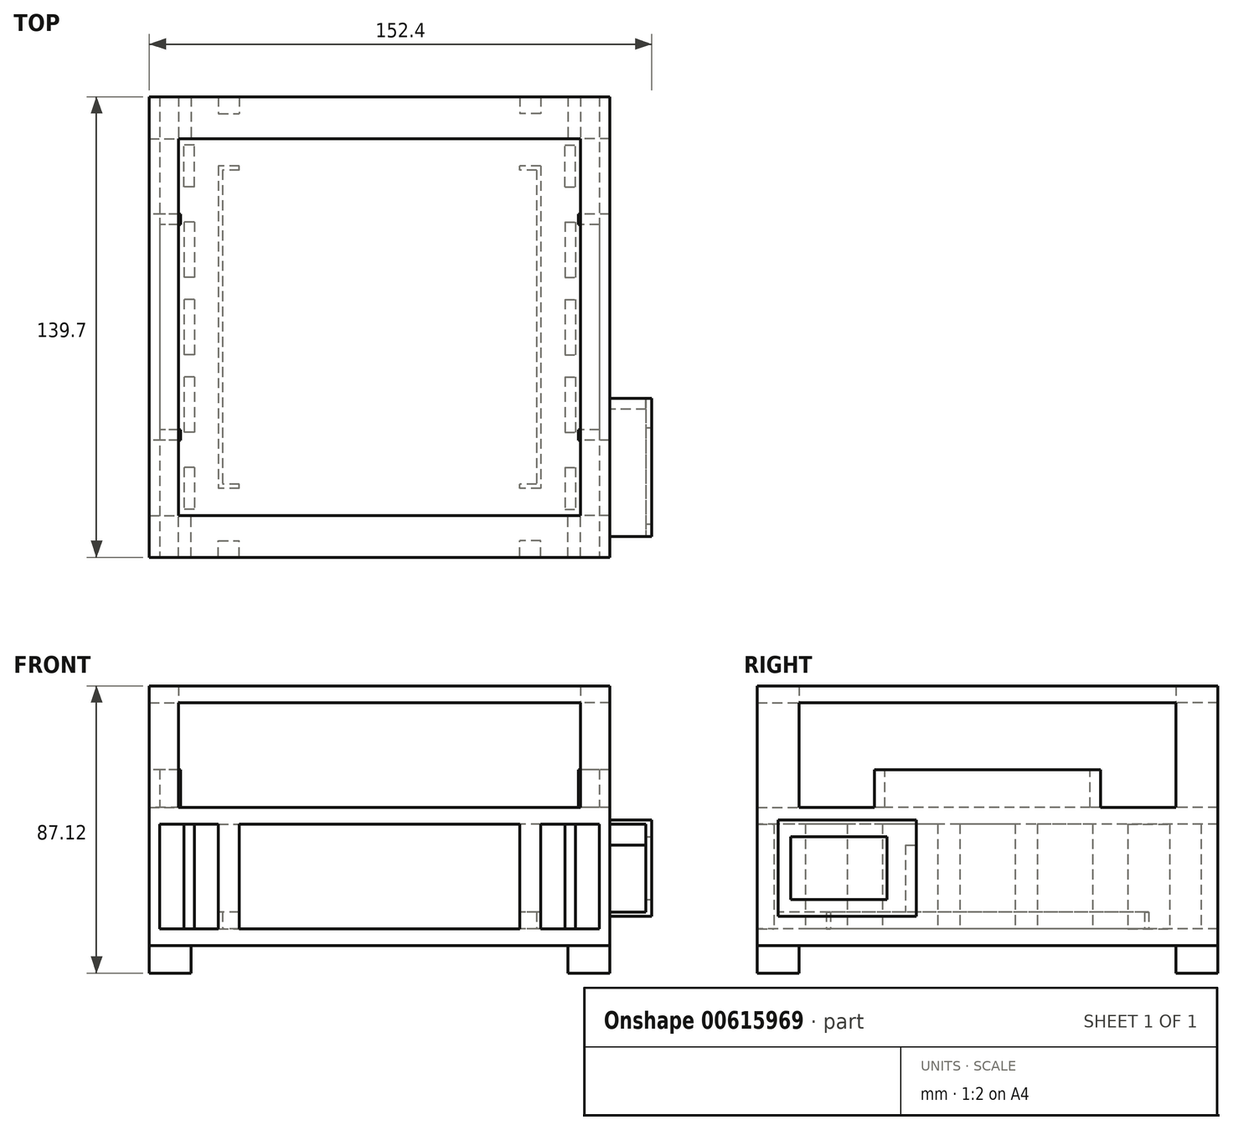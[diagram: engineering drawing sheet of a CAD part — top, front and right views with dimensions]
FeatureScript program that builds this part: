
annotation { "Feature Type Name" : "Feature", "Feature Type Description" : "" }
export const myFeature = defineFeature(function(context is Context, id is Id, definition is map)
    precondition{}
    {
        {
            var Q0;
            Q0=qCreatedBy(makeId("Top.planeOp"),FACE);
            var sketch = newSketch(context, id + "F0", { "sketchPlane" : qUnion([Q0])});
            skLineSegment(sketch, "E0.bottom", {"start": v(69.85, 69.85) * mm, "end": v(-69.85, 69.85) * mm, "construction": true});
            skLineSegment(sketch, "E0.top", {"start": v(69.85, -69.85) * mm, "end": v(-69.85, -69.85) * mm, "construction": true});
            skLineSegment(sketch, "E0.left", {"start": v(69.85, 69.85) * mm, "end": v(69.85, -69.85) * mm, "construction": true});
            skLineSegment(sketch, "E0.right", {"start": v(-69.85, 69.85) * mm, "end": v(-69.85, -69.85) * mm, "construction": true});
            skPoint(sketch, "E0.middle", {"position": v(0, 0) * mm});
            skLineSegment(sketch, "E1.bottom", {"start": v(-69.85, -69.85) * mm, "end": v(-57.15, -69.85) * mm});
            skLineSegment(sketch, "E1.top", {"start": v(-69.85, -57.15) * mm, "end": v(-57.15, -57.15) * mm});
            skLineSegment(sketch, "E1.left", {"start": v(-69.85, -69.85) * mm, "end": v(-69.85, -57.15) * mm});
            skLineSegment(sketch, "E1.right", {"start": v(-57.15, -69.85) * mm, "end": v(-57.15, -57.15) * mm});
            skLineSegment(sketch, "E2.bottom", {"start": v(69.85, -69.85) * mm, "end": v(57.15, -69.85) * mm});
            skLineSegment(sketch, "E2.top", {"start": v(69.85, -57.15) * mm, "end": v(57.15, -57.15) * mm});
            skLineSegment(sketch, "E2.left", {"start": v(69.85, -69.85) * mm, "end": v(69.85, -57.15) * mm});
            skLineSegment(sketch, "E2.right", {"start": v(57.15, -69.85) * mm, "end": v(57.15, -57.15) * mm});
            skLineSegment(sketch, "E3.bottom", {"start": v(69.85, 69.85) * mm, "end": v(57.15, 69.85) * mm});
            skLineSegment(sketch, "E3.top", {"start": v(69.85, 57.15) * mm, "end": v(57.15, 57.15) * mm});
            skLineSegment(sketch, "E3.left", {"start": v(69.85, 69.85) * mm, "end": v(69.85, 57.15) * mm});
            skLineSegment(sketch, "E3.right", {"start": v(57.15, 69.85) * mm, "end": v(57.15, 57.15) * mm});
            skLineSegment(sketch, "E4.bottom", {"start": v(-69.85, 69.85) * mm, "end": v(-57.15, 69.85) * mm});
            skLineSegment(sketch, "E4.top", {"start": v(-69.85, 57.15) * mm, "end": v(-57.15, 57.15) * mm});
            skLineSegment(sketch, "E4.left", {"start": v(-69.85, 69.85) * mm, "end": v(-69.85, 57.15) * mm});
            skLineSegment(sketch, "E4.right", {"start": v(-57.15, 69.85) * mm, "end": v(-57.15, 57.15) * mm});
            skSolve(sketch);
        }
        {
            var Q0;
            Q0=qSketchRegion(id+"F0",true);
            extrude(context, id + "F1", {"entities" : qUnion([Q0]), "depth" : 8.38 * mm});
        }
        {
            var Q0;
            Q0=makeQuery(id+"F1.opExtrude","CAP_FACE",FACE,{"disambiguationData":[OSD([sQuery(id+"F0.wireOp",EDGE,"E1.bottom"),sQuery(id+"F0.wireOp",EDGE,"E1.top"),sQuery(id+"F0.wireOp",EDGE,"E1.left"),sQuery(id+"F0.wireOp",EDGE,"E1.right")])],"isStart":false});
            var sketch = newSketch(context, id + "F2", { "sketchPlane" : qUnion([Q0])});
            skLineSegment(sketch, "E5.bottom", {"start": v(-69.85, -69.85) * mm, "end": v(69.85, -69.85) * mm});
            skLineSegment(sketch, "E5.top", {"start": v(-69.85, 69.85) * mm, "end": v(69.85, 69.85) * mm});
            skLineSegment(sketch, "E5.left", {"start": v(-69.85, -69.85) * mm, "end": v(-69.85, 69.85) * mm});
            skLineSegment(sketch, "E5.right", {"start": v(69.85, -69.85) * mm, "end": v(69.85, 69.85) * mm});
            skSolve(sketch);
        }
        {
            var Q0;
            Q0=qSketchRegion(id+"F2",true);
            extrude(context, id + "F3", {"entities" : qUnion([Q0]), "depth" : 5.08 * mm});
        }
        {
            var Q0;
            Q0=makeQuery(id+"F3.opExtrude","CAP_FACE",FACE,{"disambiguationData":[OSD([sQuery(id+"F2.wireOp",EDGE,"E5.bottom"),sQuery(id+"F2.wireOp",EDGE,"E5.top"),sQuery(id+"F2.wireOp",EDGE,"E5.left"),sQuery(id+"F2.wireOp",EDGE,"E5.right")])],"isStart":false});
            var sketch = newSketch(context, id + "F4", { "sketchPlane" : qUnion([Q0])});
            skSolve(sketch);
        }
        {
            var Q0;
            Q0=makeQuery(id+"F4.imprint","IMPRINT",FACE,{"disambiguationData":[TD([[makeQuery(id+"F4.imprint","IMPRINT",EDGE,{"derivedFrom":makeQuery(id+"F3.opExtrude","CAP_EDGE",EDGE,{"disambiguationData":[OSD([sQuery(id+"F2.wireOp",EDGE,"E5.bottom")])],"isStart":false})}),1.0]])]});
            var sketch = newSketch(context, id + "F5", { "sketchPlane" : qUnion([Q0])});
            skLineSegment(sketch, "E6.bottom", {"start": v(47.62, 47.63) * mm, "end": v(-47.63, 47.63) * mm});
            skLineSegment(sketch, "E6.top", {"start": v(47.63, -47.63) * mm, "end": v(-47.62, -47.63) * mm});
            skLineSegment(sketch, "E6.left", {"start": v(47.62, 47.63) * mm, "end": v(47.63, -47.63) * mm});
            skLineSegment(sketch, "E6.right", {"start": v(-47.63, 47.63) * mm, "end": v(-47.62, -47.63) * mm});
            skPoint(sketch, "E6.middle", {"position": v(0, 0) * mm});
            skLineSegment(sketch, "E7.bottom", {"start": v(48.9, 48.9) * mm, "end": v(-48.9, 48.9) * mm});
            skLineSegment(sketch, "E7.top", {"start": v(48.9, -48.9) * mm, "end": v(-48.9, -48.9) * mm});
            skLineSegment(sketch, "E7.left", {"start": v(48.9, 48.9) * mm, "end": v(48.9, -48.9) * mm});
            skLineSegment(sketch, "E7.right", {"start": v(-48.9, 48.9) * mm, "end": v(-48.9, -48.9) * mm});
            skSolve(sketch);
        }
        {
            var Q0;
            Q0=qSketchRegion(id+"F5",true);
            extrude(context, id + "F6", {"entities" : qUnion([Q0]), "operationType" : NewBodyOperationType.ADD, "depth" : 5.08 * mm});
        }
        {
            var Q0;
            Q0=makeQuery(id+"F4.imprint","IMPRINT",FACE,{"disambiguationData":[TD([[makeQuery(id+"F4.imprint","IMPRINT",EDGE,{"derivedFrom":makeQuery(id+"F3.opExtrude","CAP_EDGE",EDGE,{"disambiguationData":[OSD([sQuery(id+"F2.wireOp",EDGE,"E5.bottom")])],"isStart":false})}),1.0]])]});
            var sketch = newSketch(context, id + "F7", { "sketchPlane" : qUnion([Q0])});
            skLineSegment(sketch, "E8.bottom", {"start": v(42.55, -69.85) * mm, "end": v(-42.54, -69.85) * mm});
            skLineSegment(sketch, "E8.top", {"start": v(42.54, 69.85) * mm, "end": v(-42.55, 69.85) * mm});
            skLineSegment(sketch, "E8.left", {"start": v(42.55, -69.85) * mm, "end": v(42.54, 69.85) * mm});
            skLineSegment(sketch, "E8.right", {"start": v(-42.54, -69.85) * mm, "end": v(-42.55, 69.85) * mm});
            skPoint(sketch, "E8.middle", {"position": v(0, 0) * mm});
            skSolve(sketch);
        }
        {
            var Q0;
            Q0=qSketchRegion(id+"F7",true);
            extrude(context, id + "F8", {"entities" : qUnion([Q0]), "operationType" : NewBodyOperationType.REMOVE, "depth" : 5.08 * mm});
        }
        {
            var Q0;
            Q0=makeQuery(id+"F4.imprint","IMPRINT",FACE,{"disambiguationData":[TD([[makeQuery(id+"F4.imprint","IMPRINT",EDGE,{"derivedFrom":makeQuery(id+"F3.opExtrude","CAP_EDGE",EDGE,{"disambiguationData":[OSD([sQuery(id+"F2.wireOp",EDGE,"E5.bottom")])],"isStart":false})}),1.0]])]});
            var sketch = newSketch(context, id + "F9", { "sketchPlane" : qUnion([Q0])});
            skLineSegment(sketch, "E9.bottom", {"start": v(69.85, 69.85) * mm, "end": v(-69.85, 69.85) * mm, "construction": true});
            skLineSegment(sketch, "E9.top", {"start": v(69.85, -69.85) * mm, "end": v(-69.85, -69.85) * mm, "construction": true});
            skLineSegment(sketch, "E9.left", {"start": v(69.85, 69.85) * mm, "end": v(69.85, -69.85) * mm, "construction": true});
            skLineSegment(sketch, "E9.right", {"start": v(-69.85, 69.85) * mm, "end": v(-69.85, -69.85) * mm, "construction": true});
            skPoint(sketch, "E9.middle", {"position": v(0, 0) * mm});
            skLineSegment(sketch, "E10.bottom", {"start": v(-69.85, 69.85) * mm, "end": v(-66.68, 69.85) * mm});
            skLineSegment(sketch, "E10.top", {"start": v(-69.85, -69.85) * mm, "end": v(-66.67, -69.85) * mm});
            skLineSegment(sketch, "E10.left", {"start": v(-69.85, 69.85) * mm, "end": v(-69.85, -69.85) * mm});
            skLineSegment(sketch, "E10.right", {"start": v(-66.68, 69.85) * mm, "end": v(-66.67, -69.85) * mm});
            skLineSegment(sketch, "E11.bottom", {"start": v(-48.9, -48.9) * mm, "end": v(-66.67, -48.9) * mm, "construction": true});
            skLineSegment(sketch, "E11.top", {"start": v(-48.9, 48.9) * mm, "end": v(-66.67, 48.9) * mm, "construction": true});
            skLineSegment(sketch, "E11.left", {"start": v(-48.9, -48.9) * mm, "end": v(-48.9, 48.9) * mm, "construction": true});
            skLineSegment(sketch, "E11.right", {"start": v(-66.68, -48.9) * mm, "end": v(-66.68, 48.9) * mm, "construction": true});
            skLineSegment(sketch, "E12.bottom", {"start": v(-66.67, 48.9) * mm, "end": v(-57.78, 48.9) * mm, "construction": true});
            skLineSegment(sketch, "E12.top", {"start": v(-66.67, -48.9) * mm, "end": v(-57.78, -48.9) * mm, "construction": true});
            skLineSegment(sketch, "E12.left", {"start": v(-66.68, 48.9) * mm, "end": v(-66.68, -48.9) * mm, "construction": true});
            skLineSegment(sketch, "E12.right", {"start": v(-57.78, 48.9) * mm, "end": v(-57.78, -48.9) * mm, "construction": true});
            skLineSegment(sketch, "E13.bottom", {"start": v(-66.67, 48.9) * mm, "end": v(-48.9, 48.9) * mm, "construction": true});
            skLineSegment(sketch, "E13.top", {"start": v(-66.67, 23.5) * mm, "end": v(-48.9, 23.5) * mm, "construction": true});
            skLineSegment(sketch, "E13.left", {"start": v(-66.68, 48.9) * mm, "end": v(-66.68, 23.5) * mm, "construction": true});
            skLineSegment(sketch, "E13.right", {"start": v(-48.9, 48.9) * mm, "end": v(-48.9, 23.5) * mm, "construction": true});
            skLineSegment(sketch, "E14.bottom", {"start": v(-66.67, -48.9) * mm, "end": v(-48.9, -48.9) * mm, "construction": true});
            skLineSegment(sketch, "E14.top", {"start": v(-66.67, -23.5) * mm, "end": v(-48.9, -23.5) * mm, "construction": true});
            skLineSegment(sketch, "E14.left", {"start": v(-66.68, -48.9) * mm, "end": v(-66.68, -23.5) * mm, "construction": true});
            skLineSegment(sketch, "E14.right", {"start": v(-48.9, -48.9) * mm, "end": v(-48.9, -23.5) * mm, "construction": true});
            skLineSegment(sketch, "E15.bottom", {"start": v(-56.2, 31.88) * mm, "end": v(-59.37, 31.88) * mm});
            skLineSegment(sketch, "E15.top", {"start": v(-56.2, 15.11) * mm, "end": v(-59.37, 15.11) * mm});
            skLineSegment(sketch, "E15.left", {"start": v(-56.2, 31.88) * mm, "end": v(-56.2, 15.11) * mm});
            skLineSegment(sketch, "E15.right", {"start": v(-59.37, 31.88) * mm, "end": v(-59.37, 15.11) * mm});
            skPoint(sketch, "E15.middle", {"position": v(-57.78, 23.5) * mm});
            skLineSegment(sketch, "E16.bottom", {"start": v(-56.2, 8.38) * mm, "end": v(-59.37, 8.38) * mm});
            skLineSegment(sketch, "E16.top", {"start": v(-56.2, -8.38) * mm, "end": v(-59.37, -8.38) * mm});
            skLineSegment(sketch, "E16.left", {"start": v(-56.2, 8.38) * mm, "end": v(-56.2, -8.38) * mm});
            skLineSegment(sketch, "E16.right", {"start": v(-59.37, 8.38) * mm, "end": v(-59.37, -8.38) * mm});
            skPoint(sketch, "E16.middle", {"position": v(-57.78, 0) * mm});
            skLineSegment(sketch, "E17.bottom", {"start": v(-56.2, -15.11) * mm, "end": v(-59.37, -15.11) * mm});
            skLineSegment(sketch, "E17.top", {"start": v(-56.2, -31.88) * mm, "end": v(-59.37, -31.88) * mm});
            skLineSegment(sketch, "E17.left", {"start": v(-56.2, -15.11) * mm, "end": v(-56.2, -31.88) * mm});
            skLineSegment(sketch, "E17.right", {"start": v(-59.37, -15.11) * mm, "end": v(-59.37, -31.88) * mm});
            skPoint(sketch, "E17.middle", {"position": v(-57.78, -23.5) * mm});
            skLineSegment(sketch, "E18.bottom", {"start": v(-56.2, 42.55) * mm, "end": v(-59.37, 42.55) * mm});
            skLineSegment(sketch, "E18.top", {"start": v(-56.2, 55.25) * mm, "end": v(-59.37, 55.25) * mm});
            skLineSegment(sketch, "E18.left", {"start": v(-56.2, 42.55) * mm, "end": v(-56.2, 55.25) * mm});
            skLineSegment(sketch, "E18.right", {"start": v(-59.37, 42.55) * mm, "end": v(-59.37, 55.25) * mm});
            skPoint(sketch, "E18.middle", {"position": v(-57.78, 48.9) * mm});
            skLineSegment(sketch, "E19.bottom", {"start": v(-56.2, -42.55) * mm, "end": v(-59.37, -42.55) * mm});
            skLineSegment(sketch, "E19.top", {"start": v(-56.2, -55.25) * mm, "end": v(-59.37, -55.25) * mm});
            skLineSegment(sketch, "E19.left", {"start": v(-56.2, -42.55) * mm, "end": v(-56.2, -55.25) * mm});
            skLineSegment(sketch, "E19.right", {"start": v(-59.37, -42.55) * mm, "end": v(-59.37, -55.25) * mm});
            skPoint(sketch, "E19.middle", {"position": v(-57.78, -48.9) * mm});
            skLineSegment(sketch, "E20.bottom", {"start": v(-48.9, 69.85) * mm, "end": v(-42.55, 69.85) * mm});
            skLineSegment(sketch, "E20.top", {"start": v(-48.9, 64.77) * mm, "end": v(-42.55, 64.77) * mm});
            skLineSegment(sketch, "E20.left", {"start": v(-48.9, 69.85) * mm, "end": v(-48.9, 64.77) * mm});
            skLineSegment(sketch, "E20.right", {"start": v(-42.55, 69.85) * mm, "end": v(-42.55, 64.77) * mm});
            skLineSegment(sketch, "E21.bottom", {"start": v(-48.9, -69.85) * mm, "end": v(-42.55, -69.85) * mm});
            skLineSegment(sketch, "E21.top", {"start": v(-48.9, -64.77) * mm, "end": v(-42.55, -64.77) * mm});
            skLineSegment(sketch, "E21.left", {"start": v(-48.9, -69.85) * mm, "end": v(-48.9, -64.77) * mm});
            skLineSegment(sketch, "E21.right", {"start": v(-42.55, -69.85) * mm, "end": v(-42.55, -64.77) * mm});
            skLineSegment(sketch, "E22", {"start": v(0, 69.85) * mm, "end": v(0, -69.85) * mm, "construction": true});
            skLineSegment(sketch, "E23.MirrorCS", {"start": v(56.2, 42.55) * mm, "end": v(56.2, 55.25) * mm});
            skLineSegment(sketch, "E24.MirrorCS", {"start": v(42.55, 69.85) * mm, "end": v(42.55, 64.77) * mm});
            skLineSegment(sketch, "E25.MirrorCS", {"start": v(56.2, -55.25) * mm, "end": v(59.37, -55.25) * mm});
            skLineSegment(sketch, "E26.MirrorCS", {"start": v(56.2, 15.11) * mm, "end": v(59.37, 15.11) * mm});
            skLineSegment(sketch, "E27.MirrorCS", {"start": v(48.9, -69.85) * mm, "end": v(48.9, -64.77) * mm});
            skLineSegment(sketch, "E28.MirrorCS", {"start": v(42.55, -69.85) * mm, "end": v(42.55, -64.77) * mm});
            skLineSegment(sketch, "E29.MirrorCS", {"start": v(66.67, -48.9) * mm, "end": v(57.79, -48.9) * mm, "construction": true});
            skLineSegment(sketch, "E30.MirrorCS", {"start": v(56.2, 31.88) * mm, "end": v(59.37, 31.88) * mm});
            skLineSegment(sketch, "E31.MirrorCS", {"start": v(56.2, -42.55) * mm, "end": v(59.37, -42.55) * mm});
            skLineSegment(sketch, "E32.MirrorCS", {"start": v(56.2, 55.25) * mm, "end": v(59.37, 55.25) * mm});
            skLineSegment(sketch, "E33.MirrorCS", {"start": v(48.9, 69.85) * mm, "end": v(48.9, 64.77) * mm});
            skLineSegment(sketch, "E34.MirrorCS", {"start": v(56.2, -15.11) * mm, "end": v(59.37, -15.11) * mm});
            skLineSegment(sketch, "E35.MirrorCS", {"start": v(69.85, 69.85) * mm, "end": v(66.68, 69.85) * mm});
            skLineSegment(sketch, "E36.MirrorCS", {"start": v(56.2, 42.55) * mm, "end": v(59.37, 42.55) * mm});
            skLineSegment(sketch, "E37.MirrorCS", {"start": v(56.2, 8.38) * mm, "end": v(59.37, 8.38) * mm});
            skLineSegment(sketch, "E38.MirrorCS", {"start": v(69.85, -69.85) * mm, "end": v(66.68, -69.85) * mm});
            skLineSegment(sketch, "E39.MirrorCS", {"start": v(56.2, -31.88) * mm, "end": v(59.37, -31.88) * mm});
            skLineSegment(sketch, "E40.MirrorCS", {"start": v(56.2, -8.38) * mm, "end": v(59.37, -8.38) * mm});
            skLineSegment(sketch, "E41.MirrorCS", {"start": v(56.2, -42.55) * mm, "end": v(56.2, -55.25) * mm});
            skLineSegment(sketch, "E42.MirrorCS", {"start": v(66.68, 48.9) * mm, "end": v(66.68, -48.9) * mm, "construction": true});
            skLineSegment(sketch, "E43.MirrorCS", {"start": v(48.9, 48.9) * mm, "end": v(48.9, 23.5) * mm, "construction": true});
            skLineSegment(sketch, "E44.MirrorCS", {"start": v(59.37, -42.55) * mm, "end": v(59.37, -55.25) * mm});
            skLineSegment(sketch, "E45.MirrorCS", {"start": v(66.67, 48.9) * mm, "end": v(57.78, 48.9) * mm, "construction": true});
            skLineSegment(sketch, "E46.MirrorCS", {"start": v(48.9, 48.9) * mm, "end": v(66.67, 48.9) * mm, "construction": true});
            skLineSegment(sketch, "E47.MirrorCS", {"start": v(59.37, 42.55) * mm, "end": v(59.37, 55.25) * mm});
            skLineSegment(sketch, "E48.MirrorCS", {"start": v(69.85, 69.85) * mm, "end": v(69.85, -69.85) * mm});
            skLineSegment(sketch, "E49.MirrorCS", {"start": v(48.9, -48.9) * mm, "end": v(66.67, -48.9) * mm, "construction": true});
            skLineSegment(sketch, "E50.MirrorCS", {"start": v(59.37, 8.38) * mm, "end": v(59.37, -8.38) * mm});
            skLineSegment(sketch, "E51.MirrorCS", {"start": v(66.68, -48.9) * mm, "end": v(66.68, -23.5) * mm, "construction": true});
            skLineSegment(sketch, "E52.MirrorCS", {"start": v(56.2, -15.11) * mm, "end": v(56.2, -31.88) * mm});
            skLineSegment(sketch, "E53.MirrorCS", {"start": v(59.37, -15.11) * mm, "end": v(59.37, -31.88) * mm});
            skLineSegment(sketch, "E54.MirrorCS", {"start": v(56.2, 31.88) * mm, "end": v(56.2, 15.11) * mm});
            skLineSegment(sketch, "E55.MirrorCS", {"start": v(66.68, 48.9) * mm, "end": v(66.68, 23.5) * mm, "construction": true});
            skPoint(sketch, "E56.MirrorP", {"position": v(57.78, -23.5) * mm});
            skLineSegment(sketch, "E57.MirrorCS", {"start": v(57.78, 48.9) * mm, "end": v(57.78, -48.9) * mm, "construction": true});
            skLineSegment(sketch, "E58.MirrorCS", {"start": v(56.2, 8.38) * mm, "end": v(56.2, -8.38) * mm});
            skLineSegment(sketch, "E59.MirrorCS", {"start": v(66.67, -23.5) * mm, "end": v(48.9, -23.5) * mm, "construction": true});
            skLineSegment(sketch, "E60.MirrorCS", {"start": v(48.9, -69.85) * mm, "end": v(42.55, -69.85) * mm});
            skLineSegment(sketch, "E61.MirrorCS", {"start": v(59.37, 31.88) * mm, "end": v(59.37, 15.11) * mm});
            skPoint(sketch, "E62.MirrorP", {"position": v(57.78, 23.5) * mm});
            skLineSegment(sketch, "E63.MirrorCS", {"start": v(66.67, 48.9) * mm, "end": v(48.9, 48.9) * mm, "construction": true});
            skLineSegment(sketch, "E64.MirrorCS", {"start": v(48.9, -48.9) * mm, "end": v(48.9, -23.5) * mm, "construction": true});
            skLineSegment(sketch, "E65.MirrorCS", {"start": v(66.68, 69.85) * mm, "end": v(66.68, -69.85) * mm});
            skPoint(sketch, "E66.MirrorP", {"position": v(57.78, 0) * mm});
            skLineSegment(sketch, "E67.MirrorCS", {"start": v(66.68, -48.9) * mm, "end": v(66.68, 48.9) * mm, "construction": true});
            skLineSegment(sketch, "E68.MirrorCS", {"start": v(48.9, -64.77) * mm, "end": v(42.55, -64.77) * mm});
            skLineSegment(sketch, "E69.MirrorCS", {"start": v(48.9, -48.9) * mm, "end": v(48.9, 48.9) * mm, "construction": true});
            skLineSegment(sketch, "E70.MirrorCS", {"start": v(66.67, 23.5) * mm, "end": v(48.9, 23.5) * mm, "construction": true});
            skLineSegment(sketch, "E71.MirrorCS", {"start": v(66.67, -48.9) * mm, "end": v(48.9, -48.9) * mm, "construction": true});
            skPoint(sketch, "E72.MirrorP", {"position": v(57.78, -48.9) * mm});
            skLineSegment(sketch, "E73.MirrorCS", {"start": v(48.9, 69.85) * mm, "end": v(42.55, 69.85) * mm});
            skLineSegment(sketch, "E74.MirrorCS", {"start": v(48.9, 64.77) * mm, "end": v(42.55, 64.77) * mm});
            skPoint(sketch, "E75.MirrorP", {"position": v(57.78, 48.9) * mm});
            skSolve(sketch);
        }
        {
            var Q0;
            Q0=qSketchRegion(id+"F9",true);
            extrude(context, id + "F10", {"entities" : qUnion([Q0]), "operationType" : NewBodyOperationType.ADD, "depth" : 31.75 * mm});
        }
        {
            var Q0;
            Q0=makeQuery(id+"F10.opExtrude","CAP_FACE",FACE,{"disambiguationData":[OSD([sQuery(id+"F9.wireOp",EDGE,"E10.bottom"),sQuery(id+"F9.wireOp",EDGE,"E10.top"),sQuery(id+"F9.wireOp",EDGE,"E10.left"),sQuery(id+"F9.wireOp",EDGE,"E10.right")])],"isStart":false});
            var sketch = newSketch(context, id + "F11", { "sketchPlane" : qUnion([Q0])});
            skLineSegment(sketch, "E76.bottom", {"start": v(69.85, 69.85) * mm, "end": v(-69.85, 69.85) * mm});
            skLineSegment(sketch, "E76.top", {"start": v(69.85, -69.85) * mm, "end": v(-69.85, -69.85) * mm});
            skLineSegment(sketch, "E76.left", {"start": v(69.85, 69.85) * mm, "end": v(69.85, -69.85) * mm});
            skLineSegment(sketch, "E76.right", {"start": v(-69.85, 69.85) * mm, "end": v(-69.85, -69.85) * mm});
            skPoint(sketch, "E76.middle", {"position": v(0, 0) * mm});
            skSolve(sketch);
        }
        {
            var Q0;
            Q0=qSketchRegion(id+"F11",true);
            extrude(context, id + "F12", {"entities" : qUnion([Q0]), "operationType" : NewBodyOperationType.ADD, "depth" : 5.08 * mm});
        }
        {
            var Q0;
            Q0=makeQuery(id+"F12.opExtrude","CAP_FACE",FACE,{"disambiguationData":[OSD([sQuery(id+"F11.wireOp",EDGE,"E76.bottom"),sQuery(id+"F11.wireOp",EDGE,"E76.top"),sQuery(id+"F11.wireOp",EDGE,"E76.left"),sQuery(id+"F11.wireOp",EDGE,"E76.right")])],"isStart":false});
            var sketch = newSketch(context, id + "F13", { "sketchPlane" : qUnion([Q0])});
            skLineSegment(sketch, "E77.bottom", {"start": v(66.68, 31.12) * mm, "end": v(-66.68, 31.12) * mm});
            skLineSegment(sketch, "E77.top", {"start": v(66.68, -31.12) * mm, "end": v(-66.68, -31.12) * mm});
            skLineSegment(sketch, "E77.left", {"start": v(66.68, 31.12) * mm, "end": v(66.68, -31.12) * mm});
            skLineSegment(sketch, "E77.right", {"start": v(-66.68, 31.12) * mm, "end": v(-66.68, -31.12) * mm});
            skPoint(sketch, "E77.middle", {"position": v(0, 0) * mm});
            skLineSegment(sketch, "E78.bottom", {"start": v(69.85, 34.3) * mm, "end": v(-69.85, 34.3) * mm});
            skLineSegment(sketch, "E78.top", {"start": v(69.85, -34.3) * mm, "end": v(-69.85, -34.3) * mm});
            skLineSegment(sketch, "E78.left", {"start": v(69.85, 34.3) * mm, "end": v(69.85, -34.3) * mm});
            skLineSegment(sketch, "E78.right", {"start": v(-69.85, 34.3) * mm, "end": v(-69.85, -34.3) * mm});
            skSolve(sketch);
        }
        {
            var Q0;
            Q0=qSketchRegion(id+"F13",true);
            extrude(context, id + "F14", {"entities" : qUnion([Q0]), "operationType" : NewBodyOperationType.ADD, "depth" : 11.43 * mm});
        }
        {
            var Q0;
            {var subQ0=sQuery(id+"F11.wireOp",EDGE,"E76.top");var subQ1=sQuery(id+"F11.wireOp",EDGE,"E76.left");var subQ2=sQuery(id+"F11.wireOp",EDGE,"E76.right");Q0=makeQuery(id+"F14.boolean.opBoolean","SPLIT",FACE,{"disambiguationData":[TD([makeQuery(id+"F3.opExtrude","SWEPT_FACE",FACE,{"disambiguationData":[OSD([sQuery(id+"F2.wireOp",EDGE,"E5.bottom")])]})])],"derivedFrom":makeQuery(id+"F12.opExtrude","CAP_FACE",FACE,{"disambiguationData":[OSD([sQuery(id+"F11.wireOp",EDGE,"E76.bottom"),subQ0,subQ1,subQ2])],"isStart":false})});}
            var sketch = newSketch(context, id + "F15", { "sketchPlane" : qUnion([Q0])});
            skLineSegment(sketch, "E79.bottom", {"start": v(60.32, 42.59) * mm, "end": v(-60.32, 42.59) * mm});
            skLineSegment(sketch, "E79.top", {"start": v(60.32, -42.59) * mm, "end": v(-60.32, -42.59) * mm});
            skLineSegment(sketch, "E79.left", {"start": v(60.33, 42.59) * mm, "end": v(60.33, -42.59) * mm});
            skLineSegment(sketch, "E79.right", {"start": v(-60.33, 42.59) * mm, "end": v(-60.33, -42.59) * mm});
            skPoint(sketch, "E79.middle", {"position": v(0, 0) * mm});
            skSolve(sketch);
        }
        {
            var Q0;
            Q0=qSketchRegion(id+"F15",true);
            extrude(context, id + "F16", {"entities" : qUnion([Q0]), "operationType" : NewBodyOperationType.REMOVE, "depth" : 25.4 * mm});
        }
        {
            var Q0;
            {var subQ1=sQuery(id+"F11.wireOp",EDGE,"E76.top");var subQ5=sQuery(id+"F11.wireOp",EDGE,"E76.left");var subQ7=sQuery(id+"F11.wireOp",EDGE,"E76.right");var subQ11=sQuery(id+"F11.wireOp",EDGE,"E76.bottom");var subQ12=makeQuery(id+"F12.opExtrude","CAP_FACE",FACE,{"disambiguationData":[OSD([subQ11,subQ1,subQ5,subQ7])],"isStart":false});Q0=makeQuery(id+"F16.boolean.opBoolean","MERGE",FACE,{"derivedFrom":[makeQuery(id+"F14.boolean.opBoolean","SPLIT",FACE,{"disambiguationData":[TD([makeQuery(id+"F14.opExtrude","SWEPT_FACE",FACE,{"disambiguationData":[OSD([sQuery(id+"F13.wireOp",EDGE,"E77.bottom")])]})])],"derivedFrom":subQ12}),makeQuery(id+"F14.boolean.opBoolean","SPLIT",FACE,{"disambiguationData":[TD([makeQuery(id+"F3.opExtrude","SWEPT_FACE",FACE,{"disambiguationData":[OSD([sQuery(id+"F2.wireOp",EDGE,"E5.top")])]})])],"derivedFrom":subQ12}),makeQuery(id+"F14.boolean.opBoolean","SPLIT",FACE,{"disambiguationData":[TD([makeQuery(id+"F3.opExtrude","SWEPT_FACE",FACE,{"disambiguationData":[OSD([sQuery(id+"F2.wireOp",EDGE,"E5.bottom")])]})])],"derivedFrom":subQ12}),makeQuery(id+"F16.opExtrude","CAP_FACE",FACE,{"disambiguationData":[OSD([sQuery(id+"F15.wireOp",EDGE,"E79.bottom"),sQuery(id+"F15.wireOp",EDGE,"E79.top"),sQuery(id+"F15.wireOp",EDGE,"E79.left"),sQuery(id+"F15.wireOp",EDGE,"E79.right")])],"isStart":true})]});}
            var sketch = newSketch(context, id + "F17", { "sketchPlane" : qUnion([Q0])});
            skLineSegment(sketch, "E80.bottom", {"start": v(69.85, -69.85) * mm, "end": v(-69.85, -69.85) * mm, "construction": true});
            skLineSegment(sketch, "E80.top", {"start": v(69.85, 69.85) * mm, "end": v(-69.85, 69.85) * mm, "construction": true});
            skLineSegment(sketch, "E80.left", {"start": v(69.85, -69.85) * mm, "end": v(69.85, 69.85) * mm, "construction": true});
            skLineSegment(sketch, "E80.right", {"start": v(-69.85, -69.85) * mm, "end": v(-69.85, 69.85) * mm, "construction": true});
            skPoint(sketch, "E80.middle", {"position": v(0, 0) * mm});
            skLineSegment(sketch, "E81.bottom", {"start": v(-69.85, 69.85) * mm, "end": v(-60.96, 69.85) * mm});
            skLineSegment(sketch, "E81.top", {"start": v(-69.85, 57.15) * mm, "end": v(-60.96, 57.15) * mm});
            skLineSegment(sketch, "E81.left", {"start": v(-69.85, 69.85) * mm, "end": v(-69.85, 57.15) * mm});
            skLineSegment(sketch, "E81.right", {"start": v(-60.96, 69.85) * mm, "end": v(-60.96, 57.15) * mm});
            skLineSegment(sketch, "E82.bottom", {"start": v(69.85, 69.85) * mm, "end": v(60.96, 69.85) * mm});
            skLineSegment(sketch, "E82.top", {"start": v(69.85, 57.15) * mm, "end": v(60.96, 57.15) * mm});
            skLineSegment(sketch, "E82.left", {"start": v(69.85, 69.85) * mm, "end": v(69.85, 57.15) * mm});
            skLineSegment(sketch, "E82.right", {"start": v(60.96, 69.85) * mm, "end": v(60.96, 57.15) * mm});
            skLineSegment(sketch, "E83.bottom", {"start": v(69.85, -69.85) * mm, "end": v(60.96, -69.85) * mm});
            skLineSegment(sketch, "E83.top", {"start": v(69.85, -57.15) * mm, "end": v(60.96, -57.15) * mm});
            skLineSegment(sketch, "E83.left", {"start": v(69.85, -69.85) * mm, "end": v(69.85, -57.15) * mm});
            skLineSegment(sketch, "E83.right", {"start": v(60.96, -69.85) * mm, "end": v(60.96, -57.15) * mm});
            skLineSegment(sketch, "E84.bottom", {"start": v(-69.85, -69.85) * mm, "end": v(-60.96, -69.85) * mm});
            skLineSegment(sketch, "E84.top", {"start": v(-69.85, -57.15) * mm, "end": v(-60.96, -57.15) * mm});
            skLineSegment(sketch, "E84.left", {"start": v(-69.85, -69.85) * mm, "end": v(-69.85, -57.15) * mm});
            skLineSegment(sketch, "E84.right", {"start": v(-60.96, -69.85) * mm, "end": v(-60.96, -57.15) * mm});
            skSolve(sketch);
        }
        {
            var Q0;
            Q0=qSketchRegion(id+"F17",true);
            extrude(context, id + "F18", {"entities" : qUnion([Q0]), "operationType" : NewBodyOperationType.ADD, "depth" : 31.75 * mm});
        }
        {
            var Q0;
            Q0=makeQuery(id+"F18.opExtrude","CAP_FACE",FACE,{"disambiguationData":[OSD([sQuery(id+"F17.wireOp",EDGE,"E84.bottom"),sQuery(id+"F17.wireOp",EDGE,"E84.top"),sQuery(id+"F17.wireOp",EDGE,"E84.left"),sQuery(id+"F17.wireOp",EDGE,"E84.right")])],"isStart":false});
            var sketch = newSketch(context, id + "F19", { "sketchPlane" : qUnion([Q0])});
            skLineSegment(sketch, "E85.bottom", {"start": v(-69.85, -69.85) * mm, "end": v(-60.96, -69.85) * mm});
            skLineSegment(sketch, "E85.top", {"start": v(-69.85, 69.85) * mm, "end": v(-60.96, 69.85) * mm});
            skLineSegment(sketch, "E85.left", {"start": v(-69.85, -69.85) * mm, "end": v(-69.85, 69.85) * mm});
            skLineSegment(sketch, "E85.right", {"start": v(-60.96, -69.85) * mm, "end": v(-60.96, 69.85) * mm});
            skLineSegment(sketch, "E86.bottom", {"start": v(-69.85, -69.85) * mm, "end": v(69.85, -69.85) * mm});
            skLineSegment(sketch, "E86.top", {"start": v(-69.85, -57.15) * mm, "end": v(69.85, -57.15) * mm});
            skLineSegment(sketch, "E86.left", {"start": v(-69.85, -69.85) * mm, "end": v(-69.85, -57.15) * mm});
            skLineSegment(sketch, "E86.right", {"start": v(69.85, -69.85) * mm, "end": v(69.85, -57.15) * mm});
            skLineSegment(sketch, "E87.bottom", {"start": v(-69.85, 69.85) * mm, "end": v(69.85, 69.85) * mm});
            skLineSegment(sketch, "E87.top", {"start": v(-69.85, 57.15) * mm, "end": v(69.85, 57.15) * mm});
            skLineSegment(sketch, "E87.left", {"start": v(-69.85, 69.85) * mm, "end": v(-69.85, 57.15) * mm});
            skLineSegment(sketch, "E87.right", {"start": v(69.85, 69.85) * mm, "end": v(69.85, 57.15) * mm});
            skLineSegment(sketch, "E88.bottom", {"start": v(69.85, -69.85) * mm, "end": v(60.96, -69.85) * mm});
            skLineSegment(sketch, "E88.top", {"start": v(69.85, 69.85) * mm, "end": v(60.96, 69.85) * mm});
            skLineSegment(sketch, "E88.left", {"start": v(69.85, -69.85) * mm, "end": v(69.85, 69.85) * mm});
            skLineSegment(sketch, "E88.right", {"start": v(60.96, -69.85) * mm, "end": v(60.96, 69.85) * mm});
            skSolve(sketch);
        }
        {
            var Q0;
            Q0=qSketchRegion(id+"F19",true);
            extrude(context, id + "F20", {"entities" : qUnion([Q0]), "operationType" : NewBodyOperationType.ADD, "depth" : 5.08 * mm});
        }
        {
            var Q0;
            Q0=makeQuery(id+"F20.boolean.opBoolean","MERGE",FACE,{"derivedFrom":[makeQuery(id+"F18.boolean.opBoolean","MERGE",FACE,{"derivedFrom":[makeQuery(id+"F14.boolean.opBoolean","MERGE",FACE,{"derivedFrom":[makeQuery(id+"F12.boolean.opBoolean","MERGE",FACE,{"derivedFrom":[makeQuery(id+"F10.boolean.opBoolean","MERGE",FACE,{"derivedFrom":[makeQuery(id+"F3.opExtrude","SWEPT_FACE",FACE,{"disambiguationData":[OSD([sQuery(id+"F2.wireOp",EDGE,"E5.right")])]}),makeQuery(id+"F10.opExtrude","SWEPT_FACE",FACE,{"disambiguationData":[OSD([sQuery(id+"F9.wireOp",EDGE,"E48.MirrorCS")])]})]}),makeQuery(id+"F12.opExtrude","SWEPT_FACE",FACE,{"disambiguationData":[OSD([sQuery(id+"F11.wireOp",EDGE,"E76.left")])]})]}),makeQuery(id+"F14.opExtrude","SWEPT_FACE",FACE,{"disambiguationData":[OSD([sQuery(id+"F13.wireOp",EDGE,"E78.left")])]})]}),makeQuery(id+"F18.opExtrude","SWEPT_FACE",FACE,{"disambiguationData":[OSD([sQuery(id+"F17.wireOp",EDGE,"E82.left")])]}),makeQuery(id+"F18.opExtrude","SWEPT_FACE",FACE,{"disambiguationData":[OSD([sQuery(id+"F17.wireOp",EDGE,"E83.left")])]})]}),makeQuery(id+"F20.opExtrude","SWEPT_FACE",FACE,{"disambiguationData":[OSD([sQuery(id+"F19.wireOp",EDGE,"E88.left")])]})]});
            var sketch = newSketch(context, id + "F21", { "sketchPlane" : qUnion([Q0])});
            skLineSegment(sketch, "E89.bottom", {"start": v(-69.85, 8.38) * mm, "end": v(-6.35, 8.38) * mm, "construction": true});
            skLineSegment(sketch, "E89.top", {"start": v(-69.85, 50.3) * mm, "end": v(-6.35, 50.3) * mm, "construction": true});
            skLineSegment(sketch, "E89.left", {"start": v(-69.85, 8.38) * mm, "end": v(-69.85, 50.3) * mm, "construction": true});
            skLineSegment(sketch, "E89.right", {"start": v(-6.35, 8.38) * mm, "end": v(-6.35, 50.3) * mm, "construction": true});
            skLineSegment(sketch, "E90.bottom", {"start": v(-6.35, 8.38) * mm, "end": v(-63.5, 8.38) * mm, "construction": true});
            skLineSegment(sketch, "E90.top", {"start": v(-6.35, 46.48) * mm, "end": v(-63.5, 46.48) * mm, "construction": true});
            skLineSegment(sketch, "E90.left", {"start": v(-6.35, 8.38) * mm, "end": v(-6.35, 46.48) * mm, "construction": true});
            skLineSegment(sketch, "E90.right", {"start": v(-63.5, 8.38) * mm, "end": v(-63.5, 46.48) * mm, "construction": true});
            skLineSegment(sketch, "E91.bottom", {"start": v(-63.5, 46.48) * mm, "end": v(-21.6, 46.48) * mm});
            skLineSegment(sketch, "E91.top", {"start": v(-63.5, 17.27) * mm, "end": v(-21.6, 17.27) * mm});
            skLineSegment(sketch, "E91.left", {"start": v(-63.5, 46.48) * mm, "end": v(-63.5, 17.27) * mm});
            skLineSegment(sketch, "E91.right", {"start": v(-21.6, 46.48) * mm, "end": v(-21.6, 17.27) * mm});
            skSolve(sketch);
        }
        {
            var Q0;
            Q0=qSketchRegion(id+"F21",true);
            var Q1;
            Q1=qSketchRegion(id+"F23",true);
            extrude(context, id + "F22", {"entities" : qUnion([Q0, Q1]), "operationType" : NewBodyOperationType.ADD, "depth" : 12.7 * mm});
        }
        {
            var Q0;
            Q0=makeQuery(id+"F22.opExtrude","SWEPT_FACE",FACE,{"disambiguationData":[OSD([sQuery(id+"F21.wireOp",EDGE,"E91.left")])]});
            var sketch = newSketch(context, id + "F23", { "sketchPlane" : qUnion([Q0])});
            skLineSegment(sketch, "E92.bottom", {"start": v(69.85, 45.21) * mm, "end": v(80.77, 45.21) * mm});
            skLineSegment(sketch, "E92.top", {"start": v(69.85, 18.54) * mm, "end": v(80.77, 18.54) * mm});
            skLineSegment(sketch, "E92.left", {"start": v(69.85, 45.21) * mm, "end": v(69.85, 18.54) * mm});
            skLineSegment(sketch, "E92.right", {"start": v(80.77, 45.21) * mm, "end": v(80.77, 18.54) * mm});
            skSolve(sketch);
        }
        {
            var Q0;
            Q0=qSketchRegion(id+"F23",true);
            extrude(context, id + "F24", {"entities" : qUnion([Q0]), "operationType" : NewBodyOperationType.REMOVE, "oppositeDirection" : true, "depth" : 38.6 * mm});
        }
        {
            var Q0;
            Q0=makeQuery(id+"F22.opExtrude","SWEPT_FACE",FACE,{"disambiguationData":[OSD([sQuery(id+"F21.wireOp",EDGE,"E91.right")])]});
            var sketch = newSketch(context, id + "F25", { "sketchPlane" : qUnion([Q0])});
            skLineSegment(sketch, "E93.bottom", {"start": v(-69.85, 45.21) * mm, "end": v(-80.77, 45.21) * mm});
            skLineSegment(sketch, "E93.top", {"start": v(-69.85, 38.86) * mm, "end": v(-80.77, 38.86) * mm});
            skLineSegment(sketch, "E93.left", {"start": v(-69.85, 45.21) * mm, "end": v(-69.85, 38.86) * mm});
            skLineSegment(sketch, "E93.right", {"start": v(-80.77, 45.21) * mm, "end": v(-80.77, 38.86) * mm});
            skSolve(sketch);
        }
        {
            var Q0;
            Q0=qSketchRegion(id+"F25",true);
            extrude(context, id + "F26", {"entities" : qUnion([Q0]), "operationType" : NewBodyOperationType.REMOVE, "oppositeDirection" : true, "depth" : 25.4 * mm});
        }
        {
            var Q0;
            Q0=makeQuery(id+"F22.opExtrude","CAP_FACE",FACE,{"disambiguationData":[OSD([sQuery(id+"F21.wireOp",EDGE,"E91.bottom"),sQuery(id+"F21.wireOp",EDGE,"E91.top"),sQuery(id+"F21.wireOp",EDGE,"E91.left"),sQuery(id+"F21.wireOp",EDGE,"E91.right")])],"isStart":false});
            var sketch = newSketch(context, id + "F27", { "sketchPlane" : qUnion([Q0])});
            skLineSegment(sketch, "E94.bottom", {"start": v(-59.7, 41.4) * mm, "end": v(-30.48, 41.4) * mm});
            skLineSegment(sketch, "E94.top", {"start": v(-59.7, 22.35) * mm, "end": v(-30.48, 22.35) * mm});
            skLineSegment(sketch, "E94.left", {"start": v(-59.7, 41.4) * mm, "end": v(-59.7, 22.35) * mm});
            skLineSegment(sketch, "E94.right", {"start": v(-30.48, 41.4) * mm, "end": v(-30.48, 22.35) * mm});
            skSolve(sketch);
        }
        {
            var Q0;
            Q0=qSketchRegion(id+"F27",true);
            extrude(context, id + "F28", {"entities" : qUnion([Q0]), "operationType" : NewBodyOperationType.REMOVE, "oppositeDirection" : true, "depth" : 6.35 * mm});
        }
    });
